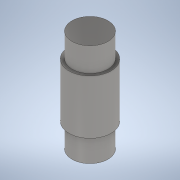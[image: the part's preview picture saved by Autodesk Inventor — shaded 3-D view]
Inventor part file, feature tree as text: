
AUTODESK INVENTOR PART (.ipt)
format: ipt  version: 2020 (Build 240168000, 168)  size: 111,104 bytes
history: native  units: mm
features: extrude x3, sketch x3
ambient origin geometry x8: Origin, YZ Plane, XZ Plane, XY Plane, X Axis, Y Axis, Z Axis, Center Point
bodies: Solid1 (feature_tree)
feature tree (6):
  extrude  "Extrusion1"  Depth=4.0mm TaperAngle=0.0deg
  extrude  "Extrusion2"  Depth=9.0mm TaperAngle=0.0deg
  extrude  "Extrusion3"  Depth=4.0mm TaperAngle=0.0deg
  sketch  "Sketch1"  dims[d0=6.0mm d1=4.0mm d2=0.0mm]
  sketch  "Sketch2"  dims[d3=7.0mm d4=9.0mm d5=0.0mm]
  sketch  "Sketch3"  dims[d6=6.0mm d7=4.0mm d8=0.0mm]
